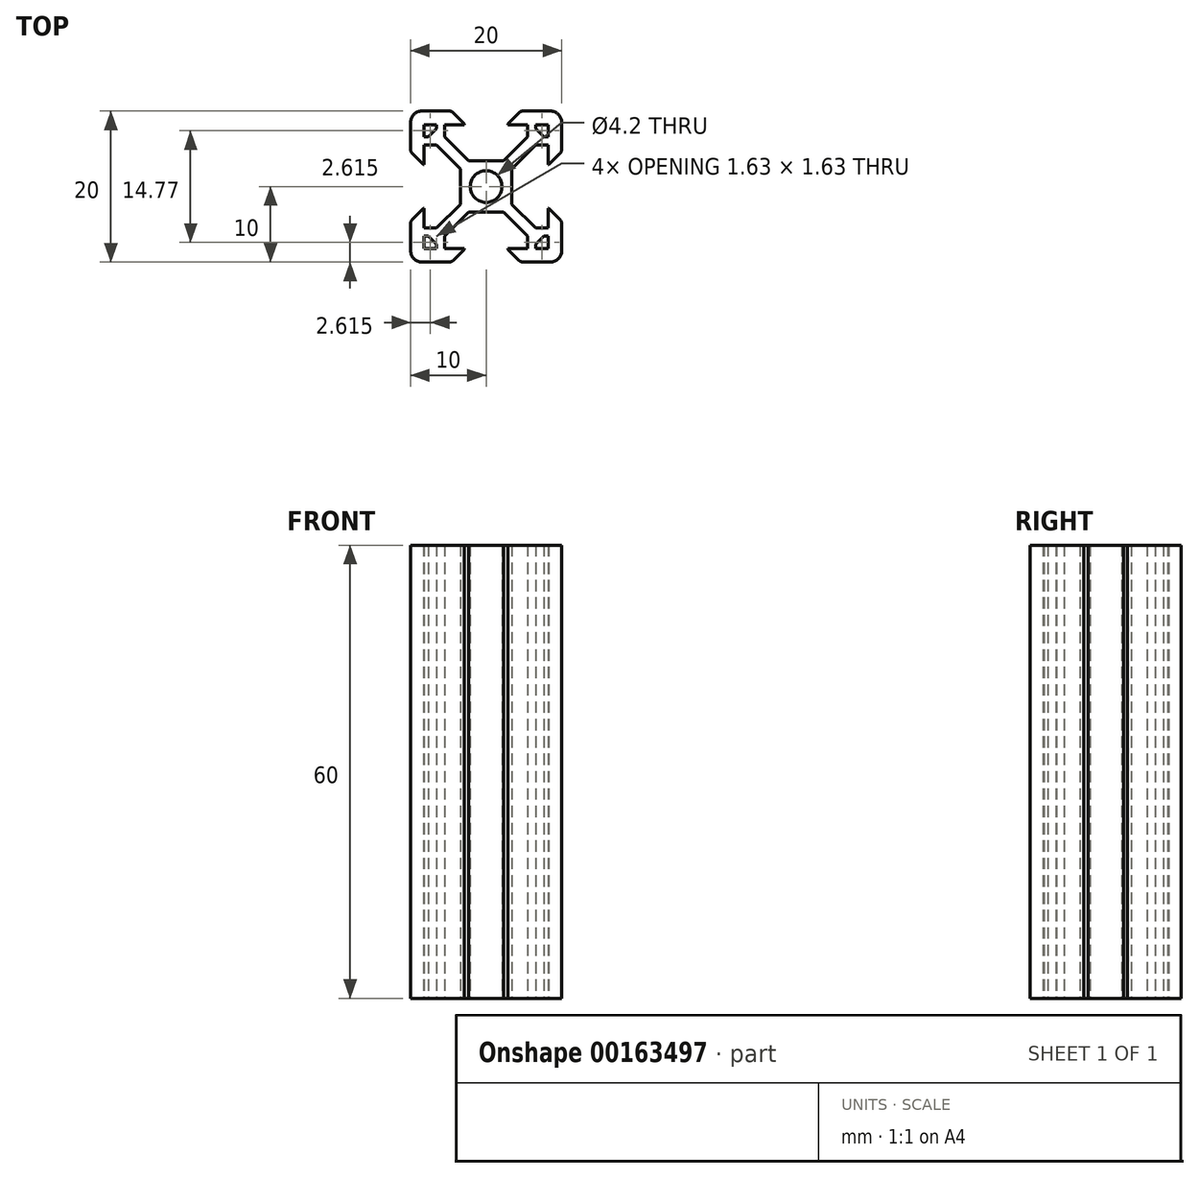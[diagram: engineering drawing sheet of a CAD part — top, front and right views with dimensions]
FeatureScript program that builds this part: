
annotation { "Feature Type Name" : "Feature", "Feature Type Description" : "" }
export const myFeature = defineFeature(function(context is Context, id is Id, definition is map)
    precondition{}
    {
        {
            var Q0;
            Q0=qCreatedBy(makeId("Top.planeOp"),FACE);
            var sketch = newSketch(context, id + "F0", { "sketchPlane" : qUnion([Q0])});
            skLineSegment(sketch, "E0", {"start": v(-8.2, -8.2) * mm, "end": v(-6.57, -8.2) * mm});
            skLineSegment(sketch, "E1", {"start": v(-8.2, -6.57) * mm, "end": v(-8.2, -8.2) * mm});
            skLineSegment(sketch, "E2", {"start": v(-7.66, -6.57) * mm, "end": v(-8.2, -6.57) * mm});
            skLineSegment(sketch, "E3", {"start": v(-6.57, -7.66) * mm, "end": v(-7.66, -6.57) * mm});
            skLineSegment(sketch, "E4", {"start": v(-6.57, -8.2) * mm, "end": v(-6.57, -7.66) * mm});
            skLineSegment(sketch, "E5", {"start": v(7.66, -6.57) * mm, "end": v(6.57, -7.66) * mm});
            skLineSegment(sketch, "E6", {"start": v(8.2, -6.57) * mm, "end": v(7.66, -6.57) * mm});
            skLineSegment(sketch, "E7", {"start": v(8.2, -8.2) * mm, "end": v(8.2, -6.57) * mm});
            skLineSegment(sketch, "E8", {"start": v(6.57, -8.2) * mm, "end": v(8.2, -8.2) * mm});
            skLineSegment(sketch, "E9", {"start": v(6.57, -7.66) * mm, "end": v(6.57, -8.2) * mm});
            skCircle(sketch, "E10", {"center": v(0, 0) * mm, "radius": 2.1 * mm});
            skLineSegment(sketch, "E11", {"start": v(8.2, 8.2) * mm, "end": v(6.57, 8.2) * mm});
            skLineSegment(sketch, "E12", {"start": v(8.2, 6.57) * mm, "end": v(8.2, 8.2) * mm});
            skLineSegment(sketch, "E13", {"start": v(7.66, 6.57) * mm, "end": v(8.2, 6.57) * mm});
            skLineSegment(sketch, "E14", {"start": v(6.57, 7.66) * mm, "end": v(7.66, 6.57) * mm});
            skLineSegment(sketch, "E15", {"start": v(6.57, 8.2) * mm, "end": v(6.57, 7.66) * mm});
            skLineSegment(sketch, "E16", {"start": v(-7.66, 6.57) * mm, "end": v(-6.57, 7.66) * mm});
            skLineSegment(sketch, "E17", {"start": v(-8.2, 6.57) * mm, "end": v(-7.66, 6.57) * mm});
            skLineSegment(sketch, "E18", {"start": v(-8.2, 8.2) * mm, "end": v(-8.2, 6.57) * mm});
            skLineSegment(sketch, "E19", {"start": v(-6.57, 8.2) * mm, "end": v(-8.2, 8.2) * mm});
            skLineSegment(sketch, "E20", {"start": v(-6.57, 7.66) * mm, "end": v(-6.57, 8.2) * mm});
            skLineSegment(sketch, "E21", {"start": v(-6.56, 5.5) * mm, "end": v(-3.4, 2.34) * mm});
            skLineSegment(sketch, "E22", {"start": v(-3.4, 2.34) * mm, "end": v(-3.4, -2.34) * mm});
            skLineSegment(sketch, "E23", {"start": v(-3.4, -2.34) * mm, "end": v(-6.56, -5.5) * mm});
            skLineSegment(sketch, "E24", {"start": v(-6.56, -5.5) * mm, "end": v(-8.2, -5.5) * mm});
            skLineSegment(sketch, "E25", {"start": v(-8.2, -5.5) * mm, "end": v(-8.2, -2.9) * mm});
            skLineSegment(sketch, "E26", {"start": v(-8.2, -2.9) * mm, "end": v(-8.31, -2.9) * mm});
            skLineSegment(sketch, "E27", {"start": v(-8.31, -2.9) * mm, "end": v(-9.77, -4.35) * mm});
            skArc(sketch, "E28", {"start": v(-9.77, -4.35) * mm, "mid": v(-9.94, -4.6) * mm, "end": v(-10, -4.9) * mm});
            skLineSegment(sketch, "E29", {"start": v(-10, -4.9) * mm, "end": v(-10, -8.5) * mm});
            skArc(sketch, "E30", {"start": v(-10, -8.5) * mm, "mid": v(-9.56, -9.56) * mm, "end": v(-8.5, -10) * mm});
            skLineSegment(sketch, "E31", {"start": v(-8.5, -10) * mm, "end": v(-4.9, -10) * mm});
            skArc(sketch, "E32", {"start": v(-4.9, -10) * mm, "mid": v(-4.6, -9.94) * mm, "end": v(-4.35, -9.77) * mm});
            skLineSegment(sketch, "E33", {"start": v(-4.35, -9.77) * mm, "end": v(-2.9, -8.31) * mm});
            skLineSegment(sketch, "E34", {"start": v(-2.9, -8.31) * mm, "end": v(-2.9, -8.2) * mm});
            skLineSegment(sketch, "E35", {"start": v(-2.9, -8.2) * mm, "end": v(-5.5, -8.2) * mm});
            skLineSegment(sketch, "E36", {"start": v(-5.5, -8.2) * mm, "end": v(-5.5, -6.56) * mm});
            skLineSegment(sketch, "E37", {"start": v(-5.5, -6.56) * mm, "end": v(-2.34, -3.4) * mm});
            skLineSegment(sketch, "E38", {"start": v(-2.34, -3.4) * mm, "end": v(2.34, -3.4) * mm});
            skLineSegment(sketch, "E39", {"start": v(2.34, -3.4) * mm, "end": v(5.5, -6.56) * mm});
            skLineSegment(sketch, "E40", {"start": v(5.5, -6.56) * mm, "end": v(5.5, -8.2) * mm});
            skLineSegment(sketch, "E41", {"start": v(5.5, -8.2) * mm, "end": v(2.9, -8.2) * mm});
            skLineSegment(sketch, "E42", {"start": v(2.9, -8.2) * mm, "end": v(2.9, -8.31) * mm});
            skLineSegment(sketch, "E43", {"start": v(2.9, -8.31) * mm, "end": v(4.35, -9.77) * mm});
            skArc(sketch, "E44", {"start": v(4.35, -9.77) * mm, "mid": v(4.6, -9.94) * mm, "end": v(4.9, -10) * mm});
            skLineSegment(sketch, "E45", {"start": v(4.9, -10) * mm, "end": v(8.5, -10) * mm});
            skArc(sketch, "E46", {"start": v(8.5, -10) * mm, "mid": v(9.56, -9.56) * mm, "end": v(10, -8.5) * mm});
            skLineSegment(sketch, "E47", {"start": v(10, -8.5) * mm, "end": v(10, -4.9) * mm});
            skArc(sketch, "E48", {"start": v(10, -4.9) * mm, "mid": v(9.94, -4.6) * mm, "end": v(9.77, -4.35) * mm});
            skLineSegment(sketch, "E49", {"start": v(9.77, -4.35) * mm, "end": v(8.31, -2.9) * mm});
            skLineSegment(sketch, "E50", {"start": v(8.31, -2.9) * mm, "end": v(8.2, -2.9) * mm});
            skLineSegment(sketch, "E51", {"start": v(8.2, -2.9) * mm, "end": v(8.2, -5.5) * mm});
            skLineSegment(sketch, "E52", {"start": v(8.2, -5.5) * mm, "end": v(6.56, -5.5) * mm});
            skLineSegment(sketch, "E53", {"start": v(6.56, -5.5) * mm, "end": v(3.4, -2.34) * mm});
            skLineSegment(sketch, "E54", {"start": v(3.4, -2.34) * mm, "end": v(3.4, 2.34) * mm});
            skLineSegment(sketch, "E55", {"start": v(3.4, 2.34) * mm, "end": v(6.56, 5.5) * mm});
            skLineSegment(sketch, "E56", {"start": v(6.56, 5.5) * mm, "end": v(8.2, 5.5) * mm});
            skLineSegment(sketch, "E57", {"start": v(8.2, 5.5) * mm, "end": v(8.2, 2.9) * mm});
            skLineSegment(sketch, "E58", {"start": v(8.2, 2.9) * mm, "end": v(8.31, 2.9) * mm});
            skLineSegment(sketch, "E59", {"start": v(8.31, 2.9) * mm, "end": v(9.77, 4.35) * mm});
            skArc(sketch, "E60", {"start": v(9.77, 4.35) * mm, "mid": v(9.94, 4.6) * mm, "end": v(10, 4.9) * mm});
            skLineSegment(sketch, "E61", {"start": v(10, 4.9) * mm, "end": v(10, 8.5) * mm});
            skArc(sketch, "E62", {"start": v(10, 8.5) * mm, "mid": v(9.56, 9.56) * mm, "end": v(8.5, 10) * mm});
            skLineSegment(sketch, "E63", {"start": v(8.5, 10) * mm, "end": v(4.9, 10) * mm});
            skArc(sketch, "E64", {"start": v(4.9, 10) * mm, "mid": v(4.6, 9.94) * mm, "end": v(4.35, 9.77) * mm});
            skLineSegment(sketch, "E65", {"start": v(4.35, 9.77) * mm, "end": v(2.9, 8.31) * mm});
            skLineSegment(sketch, "E66", {"start": v(2.9, 8.31) * mm, "end": v(2.9, 8.2) * mm});
            skLineSegment(sketch, "E67", {"start": v(2.9, 8.2) * mm, "end": v(5.5, 8.2) * mm});
            skLineSegment(sketch, "E68", {"start": v(5.5, 8.2) * mm, "end": v(5.5, 6.56) * mm});
            skLineSegment(sketch, "E69", {"start": v(5.5, 6.56) * mm, "end": v(2.34, 3.4) * mm});
            skLineSegment(sketch, "E70", {"start": v(2.34, 3.4) * mm, "end": v(-2.34, 3.4) * mm});
            skLineSegment(sketch, "E71", {"start": v(-2.34, 3.4) * mm, "end": v(-5.5, 6.56) * mm});
            skLineSegment(sketch, "E72", {"start": v(-5.5, 6.56) * mm, "end": v(-5.5, 8.2) * mm});
            skLineSegment(sketch, "E73", {"start": v(-5.5, 8.2) * mm, "end": v(-2.9, 8.2) * mm});
            skLineSegment(sketch, "E74", {"start": v(-2.9, 8.2) * mm, "end": v(-2.9, 8.31) * mm});
            skLineSegment(sketch, "E75", {"start": v(-2.9, 8.31) * mm, "end": v(-4.35, 9.77) * mm});
            skArc(sketch, "E76", {"start": v(-4.35, 9.77) * mm, "mid": v(-4.6, 9.94) * mm, "end": v(-4.9, 10) * mm});
            skLineSegment(sketch, "E77", {"start": v(-4.9, 10) * mm, "end": v(-8.5, 10) * mm});
            skArc(sketch, "E78", {"start": v(-8.5, 10) * mm, "mid": v(-9.56, 9.56) * mm, "end": v(-10, 8.5) * mm});
            skLineSegment(sketch, "E79", {"start": v(-10, 8.5) * mm, "end": v(-10, 4.9) * mm});
            skArc(sketch, "E80", {"start": v(-10, 4.9) * mm, "mid": v(-9.94, 4.6) * mm, "end": v(-9.77, 4.35) * mm});
            skLineSegment(sketch, "E81", {"start": v(-9.77, 4.35) * mm, "end": v(-8.31, 2.9) * mm});
            skLineSegment(sketch, "E82", {"start": v(-8.31, 2.9) * mm, "end": v(-8.2, 2.9) * mm});
            skLineSegment(sketch, "E83", {"start": v(-8.2, 2.9) * mm, "end": v(-8.2, 5.5) * mm});
            skLineSegment(sketch, "E84", {"start": v(-8.2, 5.5) * mm, "end": v(-6.56, 5.5) * mm});
            skSolve(sketch);
        }
        {
            var Q0;
            Q0=qSketchRegion(id+"F0",true);
            extrude(context, id + "F1", {"entities" : qUnion([Q0]), "depth" : 60 * mm});
        }
    });
